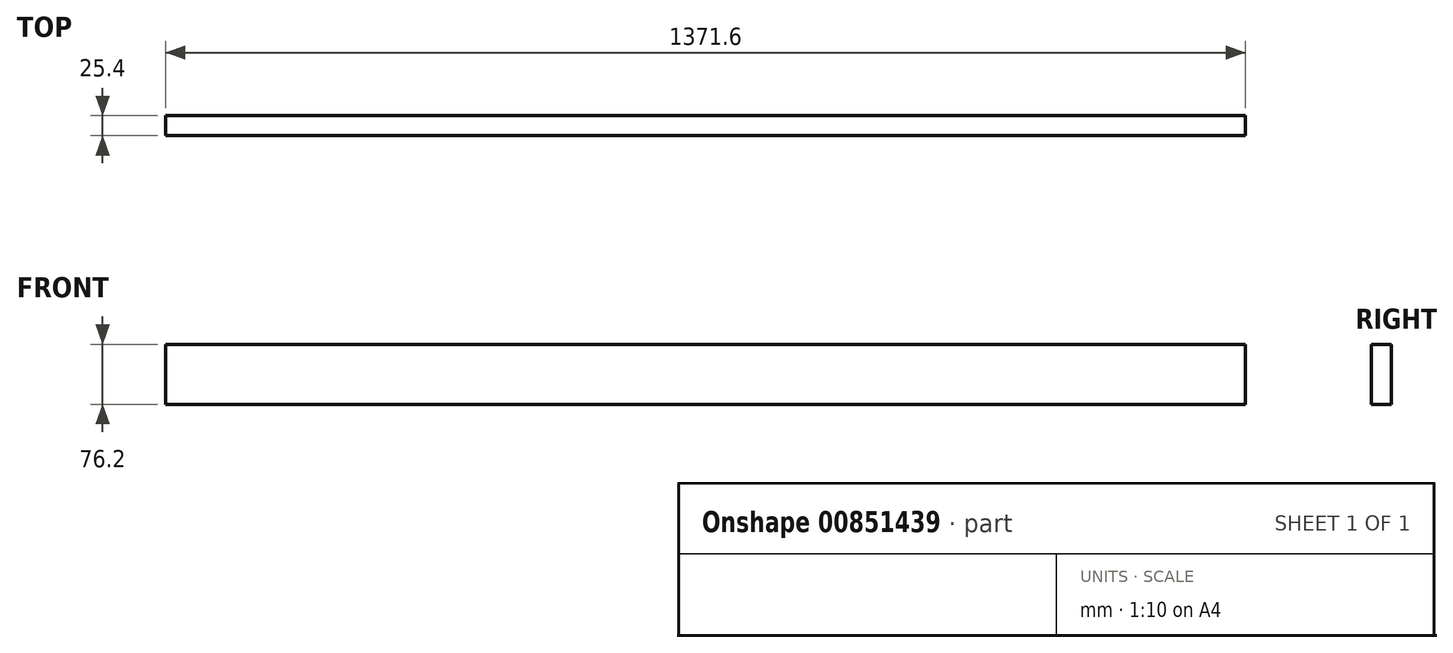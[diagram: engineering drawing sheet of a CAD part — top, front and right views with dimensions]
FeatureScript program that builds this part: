
annotation { "Feature Type Name" : "Feature", "Feature Type Description" : "" }
export const myFeature = defineFeature(function(context is Context, id is Id, definition is map)
    precondition{}
    {
        {
            var Q0;
            Q0=qCreatedBy(makeId("Front.planeOp"),FACE);
            var sketch = newSketch(context, id + "F0", { "sketchPlane" : qUnion([Q0])});
            skLineSegment(sketch, "E0", {"start": v(0, 0) * mm, "end": v(1371.6, 0) * mm});
            skLineSegment(sketch, "E1", {"start": v(1371.6, 0) * mm, "end": v(1371.6, 76.2) * mm});
            skLineSegment(sketch, "E2", {"start": v(1371.6, 76.2) * mm, "end": v(0, 76.2) * mm});
            skLineSegment(sketch, "E3", {"start": v(0, 76.2) * mm, "end": v(0, 0) * mm});
            skSolve(sketch);
        }
        {
            var Q0;
            Q0 = qSketchRegion(id + "F0", true);
            extrude(context, id + "F1", {"entities" : qUnion([Q0]), "depth" : 25.4 * mm, "offsetDistance" : 25.4 * mm});
        }
    });
